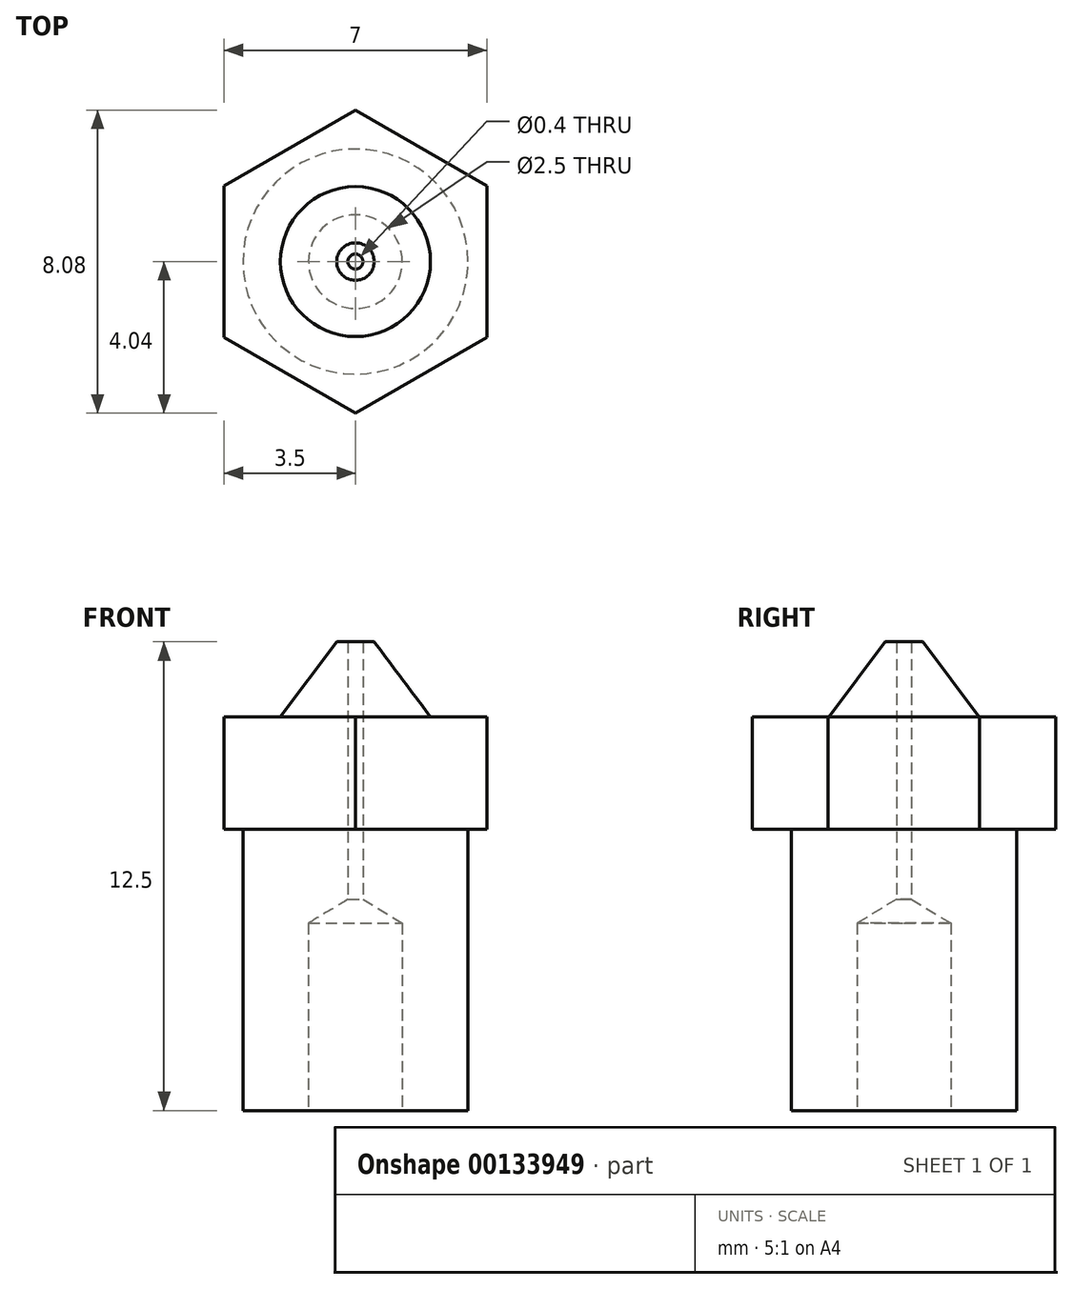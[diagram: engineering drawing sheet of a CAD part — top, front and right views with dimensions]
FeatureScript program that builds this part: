
annotation { "Feature Type Name" : "Feature", "Feature Type Description" : "" }
export const myFeature = defineFeature(function(context is Context, id is Id, definition is map)
    precondition{}
    {
        {
            var Q0;
            Q0=qCreatedBy(makeId("Top.planeOp"),FACE);
            var sketch = newSketch(context, id + "F0", { "sketchPlane" : qUnion([Q0])});
            skCircle(sketch, "E0", {"center": v(0, 0) * mm, "radius": 3 * mm});
            skSolve(sketch);
        }
        {
            var Q0;
            Q0=makeQuery(id+"F0.imprint","IMPRINT",FACE,{"disambiguationData":[TD([[makeQuery(id+"F0.imprint","IMPRINT",EDGE,{"derivedFrom":sQuery(id+"F0.wireOp",EDGE,"E0")}),1.0]])]});
            var sketch = newSketch(context, id + "F1", { "sketchPlane" : qUnion([Q0])});
            skSolve(sketch);
        }
        {
            var Q0;
            Q0 = qSketchRegion(id + "F1", true);
            var Q1;
            Q1=makeQuery(id+"F1.imprint","IMPRINT",FACE,{"disambiguationData":[TD([[makeQuery(id+"F1.imprint","IMPRINT",EDGE,{"derivedFrom":makeQuery(id+"F0.imprint","IMPRINT",EDGE,{"derivedFrom":sQuery(id+"F0.wireOp",EDGE,"E0")})}),1.0]])]});
            extrude(context, id + "F2", {"entities" : qUnion([Q0, Q1]), "depth" : 7.5 * mm, "offsetDistance" : 25 * mm});
        }
        {
            var Q0;
            Q0=makeQuery(id+"F2.opExtrude","CAP_FACE",FACE,{"disambiguationData":[OSD([sQuery(id+"F0.wireOp",EDGE,"E0")])],"isStart":false});
            var sketch = newSketch(context, id + "F3", { "sketchPlane" : qUnion([Q0])});
            skCircle(sketch, "E1.cCircle", {"center": v(0, 0) * mm, "radius": 3.5 * mm, "construction": true});
            skLineSegment(sketch, "E1.0", {"start": v(3.5, 2.02) * mm, "end": v(3.5, -2.02) * mm});
            skLineSegment(sketch, "E1.1", {"start": v(3.5, -2.02) * mm, "end": v(0, -4.04) * mm});
            skLineSegment(sketch, "E1.2", {"start": v(0, -4.04) * mm, "end": v(-3.5, -2.02) * mm});
            skLineSegment(sketch, "E1.3", {"start": v(-3.5, -2.02) * mm, "end": v(-3.5, 2.02) * mm});
            skLineSegment(sketch, "E1.4", {"start": v(-3.5, 2.02) * mm, "end": v(0, 4.04) * mm});
            skLineSegment(sketch, "E1.5", {"start": v(0, 4.04) * mm, "end": v(3.5, 2.02) * mm});
            skPoint(sketch, "E1.0.midPoint", {"position": v(3.5, 0) * mm});
            skSolve(sketch);
        }
        {
            var Q0;
            Q0=makeQuery(id+"F3.imprint","IMPRINT",FACE,{"disambiguationData":[TD([[makeQuery(id+"F3.imprint","IMPRINT",EDGE,{"derivedFrom":sQuery(id+"F3.wireOp",EDGE,"E1.0")}),-1.0]])]});
            var Q1;
            Q1=makeQuery(id+"F3.imprint","IMPRINT",FACE,{"disambiguationData":[TD([[makeQuery(id+"F3.imprint","IMPRINT",EDGE,{"derivedFrom":makeQuery(id+"F2.opExtrude","CAP_EDGE",EDGE,{"disambiguationData":[OSD([sQuery(id+"F0.wireOp",EDGE,"E0")])],"isStart":false})}),1.0]])]});
            extrude(context, id + "F4", {"entities" : qUnion([Q0, Q1]), "operationType" : NewBodyOperationType.ADD, "depth" : 3 * mm, "offsetDistance" : 25 * mm});
        }
        {
            var Q0;
            Q0=makeQuery(id+"F4.opExtrude","CAP_FACE",FACE,{"disambiguationData":[OSD([sQuery(id+"F3.wireOp",EDGE,"E1.0"),sQuery(id+"F3.wireOp",EDGE,"E1.1"),sQuery(id+"F3.wireOp",EDGE,"E1.2"),sQuery(id+"F3.wireOp",EDGE,"E1.3"),sQuery(id+"F3.wireOp",EDGE,"E1.4"),sQuery(id+"F3.wireOp",EDGE,"E1.5")])],"isStart":false});
            var sketch = newSketch(context, id + "F5", { "sketchPlane" : qUnion([Q0])});
            skCircle(sketch, "E2", {"center": v(0, 0) * mm, "radius": 2 * mm});
            skSolve(sketch);
        }
        {
            var Q0;
            Q0=makeQuery(id+"F5.imprint","IMPRINT",FACE,{"disambiguationData":[TD([[makeQuery(id+"F5.imprint","IMPRINT",EDGE,{"derivedFrom":sQuery(id+"F5.wireOp",EDGE,"E2")}),1.0]])]});
            extrude(context, id + "F6", {"entities" : qUnion([Q0]), "operationType" : NewBodyOperationType.ADD, "depth" : 2 * mm, "offsetDistance" : 25 * mm});
        }
        {
            var Q0;
            Q0=makeQuery(id+"F6.opExtrude","CAP_EDGE",EDGE,{"disambiguationData":[OSD([sQuery(id+"F5.wireOp",EDGE,"E2")])],"isStart":false});
            chamfer(context, id + "F7", {"entities" : qUnion([Q0]), "chamferType" : ChamferType.TWO_OFFSETS, "width1" : 1.5 * mm, "oppositeDirection" : false, "width2" : 2 * mm, "tangentPropagation" : true});
        }
        {
            var Q0;
            Q0=sQuery(id+"F0.wireOp",VERTEX,"E0.center");
            var Q1;
            Q1=makeQuery(id+"F2.opExtrude","SWEPT_BODY",BODY,{"disambiguationData":[OSD([sQuery(id+"F0.wireOp",EDGE,"E0")])]});
            hole(context, id + "F8", {"style" : HoleStyle.SIMPLE, "endStyle" : HoleEndStyle.THROUGH, "oppositeDirection" : true, "holeDiameter" : 0.4 * mm, "majorDiameter" : 5 * mm, "tappedDepth" : 12 * mm, "tapClearance" : 3, "startFromSketch" : true, "locations" : qUnion([Q0]), "scope" : qUnion([Q1])});
        }
        {
            var Q0;
            Q0=makeQuery(id+"F2.opExtrude","CAP_FACE",FACE,{"disambiguationData":[OSD([sQuery(id+"F0.wireOp",EDGE,"E0")])],"isStart":true});
            var sketch = newSketch(context, id + "F9", { "sketchPlane" : qUnion([Q0])});
            skPoint(sketch, "E3", {"position": v(0, 0) * mm});
            skSolve(sketch);
        }
        {
            var Q0;
            Q0=sQuery(id+"F9.wireOp",VERTEX,"E3");
            var Q1;
            Q1=makeQuery(id+"F2.opExtrude","SWEPT_BODY",BODY,{"disambiguationData":[OSD([sQuery(id+"F0.wireOp",EDGE,"E0")])]});
            hole(context, id + "F10", {"style" : HoleStyle.SIMPLE, "endStyle" : HoleEndStyle.BLIND, "holeDiameter" : 2.5 * mm, "majorDiameter" : 5 * mm, "holeDepth" : 5 * mm, "tappedDepth" : 12 * mm, "tapClearance" : 3, "startFromSketch" : true, "locations" : qUnion([Q0]), "scope" : qUnion([Q1])});
        }
    });
